# Revit family: Accessory-Grab_Bars-KOHLER-Purist-K-11890
name_source: partatom
category: Specialty Equipment
revit_build: Autodesk Revit 2015 (Build: 20140606_1530(x64)
units: mm (PartAtom-declared; Revit-internal decimal feet)

## types (5) — shared parameters
ADA Compliant = Yes
Assembly Code = C1030200
Date Modified = 1/31/2018
Default Elevation = 42"
Description = 9 inch grab bar
Height = 2 3/4"
Length = 11 13/32"
Manufacturer = KOHLER Co.
MasterFormat 1995 = 10820
MasterFormat 2004 = 10.28.13
Material = Premium Metal Construction
Product Documentation Link = http://www.us.kohler.com
Product Name = Purist
Product Page URL = http://www.us.kohler.com
URL = https://www.us.kohler.com
Width = 2 7/16"

## per-type parameters (varying)
| type | Finish | Model | Type |
| S-Polished Stainless | Kohler-Metal-S-Polished_Stainless | K-11890-S | 1 |
| BN-Vibrant Brushed Nickel | Kohler-Metal-BN-Vibrant_Brushed_Nickel | K-11890-BN | 3 |
| BS-Brushed Stainless | Kohler-Metal-BS-Brushed_Stainless | K-11890-BS | 4 |
| BV-Vibrant Brushed Bronze | Kohler-Metal-BV-Brushed_Bronze | K-11890-BV | 5 |
| TT-Vibrant Titanium | Kohler-Metal-TT-Vibrant_Titanium | K-11890-TT | 6 |

## geometry (parser evidence)
native form markers: Sweep x6
no freeform markers — native parametric forms only
